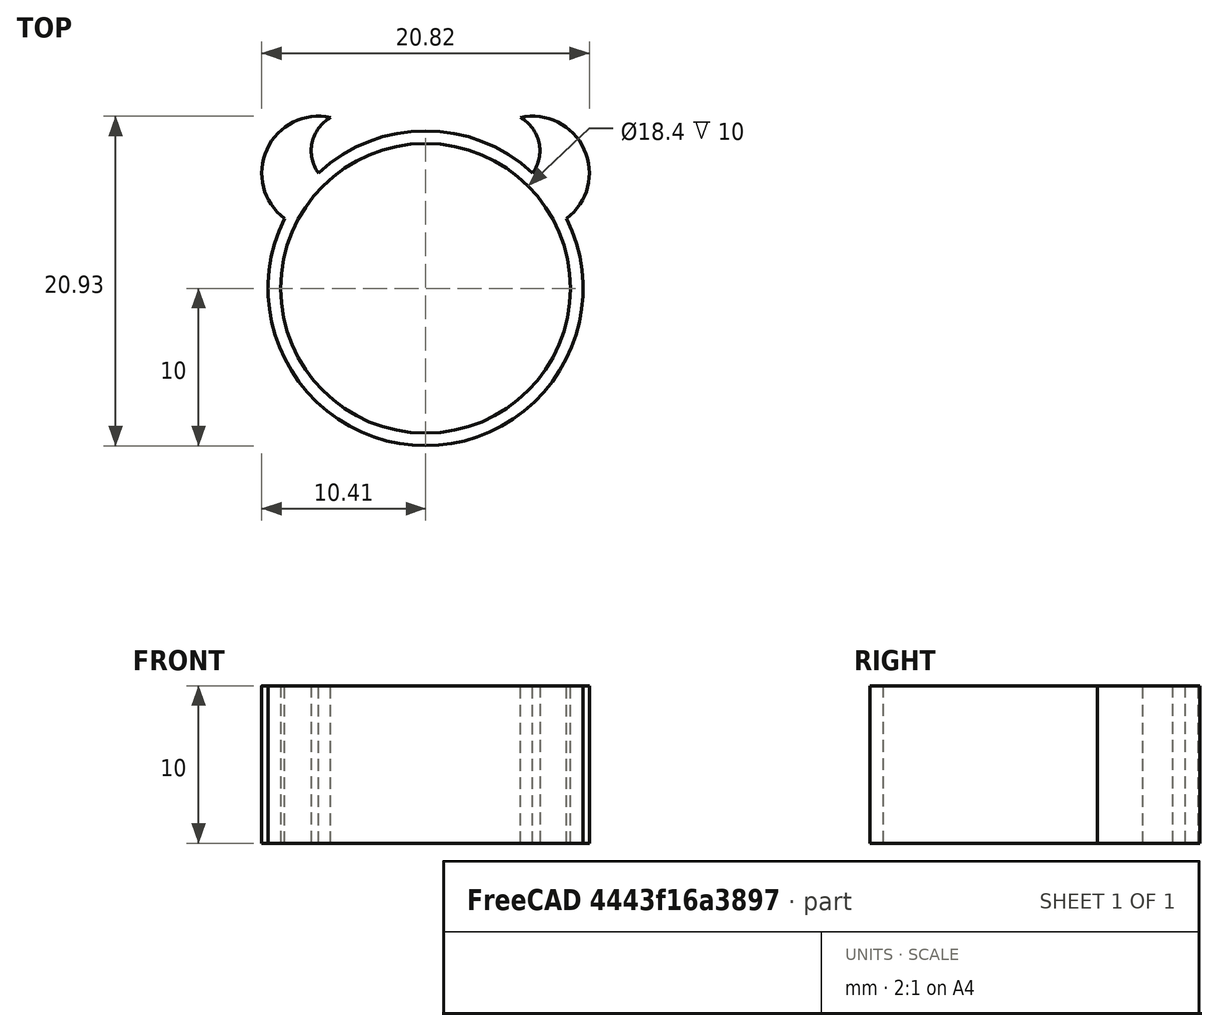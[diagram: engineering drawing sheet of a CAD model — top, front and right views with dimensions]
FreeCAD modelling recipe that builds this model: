
FCSTD DOCUMENT  (FreeCAD 0.20R29410 (Git))
Label: reto_7_mal?
License: Creative Commons Attribution-ShareAlike
LicenseURL: http://creativecommons.org/licenses/by-sa/4.0/
objects: Sketcher::SketchObject×1, PartDesign::Body×1, Part::Extrusion×1
note: 3 computed .brp shape members not serialized (recipe doc carries the construction recipe); baked Part::Feature solids carry a one-line shape summary decoded from their .brp

FEATURE [Sketcher::SketchObject] Sketch
  FullyConstrained = false
  MapMode = 5
  Support = -> [XY_Plane]
  sketch-geometry (7):
    g0: Circle CenterX=0 CenterY=0 CenterZ=0 NormalX=0 NormalY=0 NormalZ=1 AngleXU=0 Radius=9.2
    g1: ArcOfCircle CenterX=-6.80691 CenterY=7.32571 CenterZ=0 NormalX=0 NormalY=0 NormalZ=1 AngleXU=0 Radius=3.6 StartAngle=1.35115 EndAngle=4.07128
    g2: ArcOfCircle CenterX=-4.8654 CenterY=8.73658 CenterZ=0 NormalX=0 NormalY=0 NormalZ=1 AngleXU=0 Radius=2.4 StartAngle=2.07388 EndAngle=3.77001
    g3: ArcOfCircle CenterX=6.80691 CenterY=7.32571 CenterZ=0 NormalX=0 NormalY=0 NormalZ=1 AngleXU=0 Radius=3.6 StartAngle=5.35349 EndAngle=8.07363
    g4: ArcOfCircle CenterX=4.8654 CenterY=8.73658 CenterZ=0 NormalX=0 NormalY=0 NormalZ=1 AngleXU=0 Radius=2.4 StartAngle=5.65477 EndAngle=7.35089
    g5: ArcOfCircle CenterX=0 CenterY=0 CenterZ=0 NormalX=0 NormalY=0 NormalZ=1 AngleXU=0 Radius=10 StartAngle=0.822091 EndAngle=2.3195
    g6: ArcOfCircle CenterX=0 CenterY=0 CenterZ=0 NormalX=0 NormalY=0 NormalZ=1 AngleXU=0 Radius=10 StartAngle=2.68147 EndAngle=6.7433
  constraints (20):
    c: Coincident(g0,g-1)
    c: Diameter(g0) = 18.4  'd_grande'
    c: Coincident(g2,g1)
    c: Coincident(g2,g1)
    c: Symmetric(g1,g3,g-2)
    c: Symmetric(g1,g3,g-2)
    c: Coincident(g4,g3)
    c: Coincident(g4,g3)
    c: Symmetric(g2,g4,g-2)
    c: Radius(g1) = 3.6  'radio_orejas'
    c: Radius(g2) = 2.4  'radio_orejas_pequeñas'
    c: Distance(g1,g3) = 17.92  'h orejas'
    c: Coincident(g5,g0)
    c: Coincident(g5,g3)
    c: Coincident(g5,g1)
    c: Coincident(g6,g0)
    c: Coincident(g6,g3)
    c: Coincident(g6,g1)
    c: Radius(g5) = 10
    c: Radius(g6) = 10
FEATURE [PartDesign::Body] Body
  Group = -> [Sketch]
  Origin = -> Origin
FEATURE [Part::Extrusion] Extrude
  Base = -> Sketch
  Dir = (0,0,1)
  DirMode = 2
  FaceMakerClass = Part::FaceMakerBullseye
  LengthFwd = 10
  LengthRev = 0
  Solid = true
  Symmetric = false
